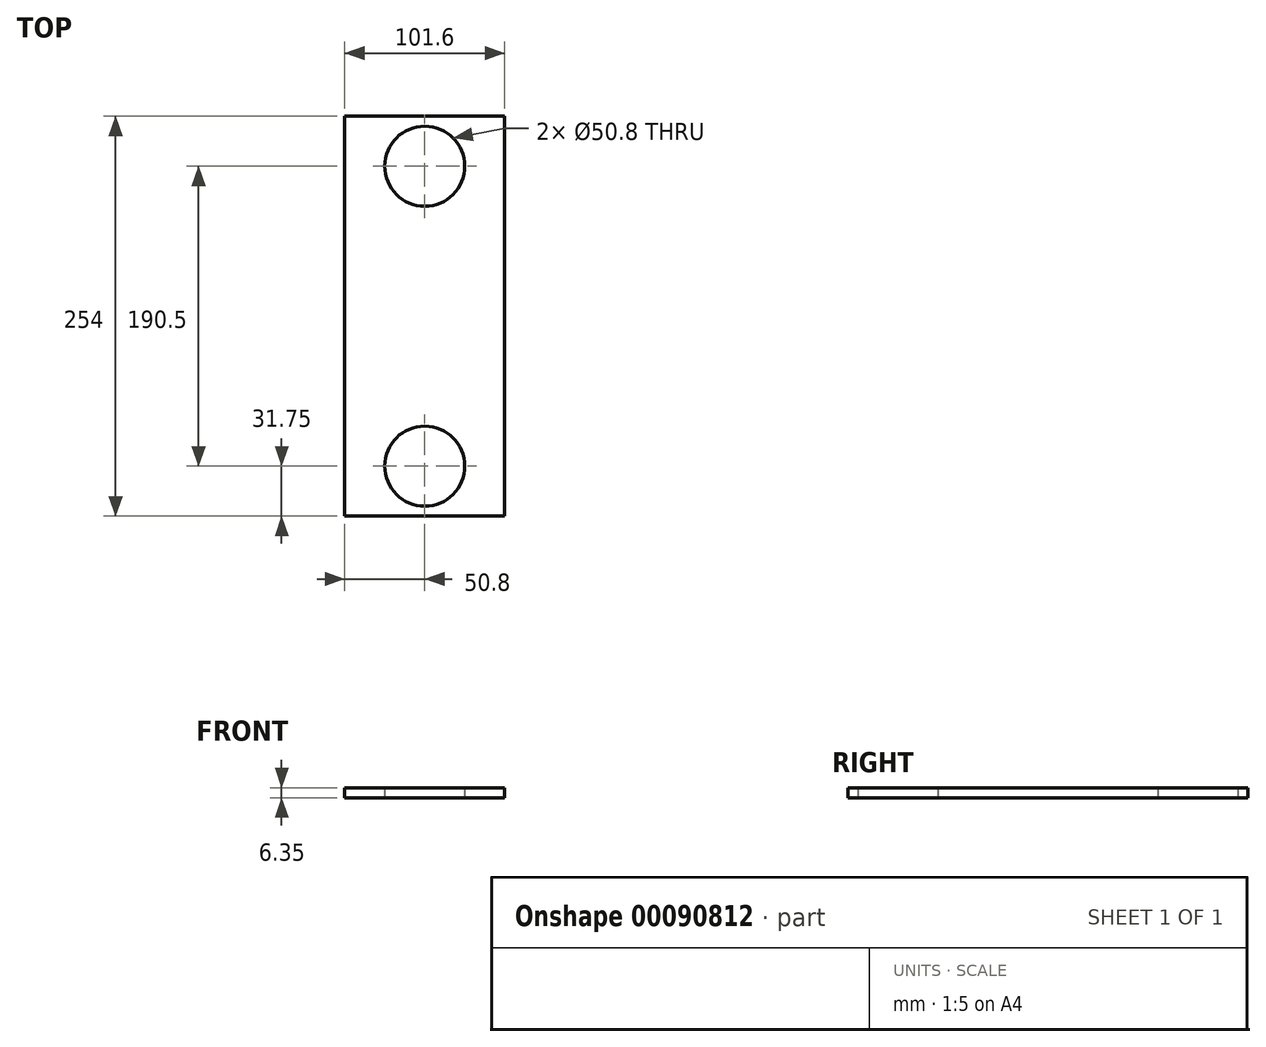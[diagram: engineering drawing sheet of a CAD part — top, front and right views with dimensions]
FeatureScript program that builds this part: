
annotation { "Feature Type Name" : "Feature", "Feature Type Description" : "" }
export const myFeature = defineFeature(function(context is Context, id is Id, definition is map)
    precondition{}
    {
        {
            var Q0;
            Q0=qCreatedBy(makeId("Top.planeOp"),FACE);
            var sketch = newSketch(context, id + "F0", { "sketchPlane" : qUnion([Q0])});
            skLineSegment(sketch, "E0.bottom", {"start": v(-37.93, 151.23) * mm, "end": v(63.67, 151.23) * mm});
            skLineSegment(sketch, "E0.top", {"start": v(-37.93, -102.77) * mm, "end": v(63.67, -102.77) * mm});
            skLineSegment(sketch, "E0.left", {"start": v(-37.93, 151.23) * mm, "end": v(-37.93, -102.77) * mm});
            skLineSegment(sketch, "E0.right", {"start": v(63.67, 151.23) * mm, "end": v(63.67, -102.77) * mm});
            skPoint(sketch, "E1", {"position": v(12.87, 151.23) * mm});
            skCircle(sketch, "E2", {"center": v(12.87, 119.48) * mm, "radius": 25.4 * mm});
            skCircle(sketch, "E3", {"center": v(12.87, -71.02) * mm, "radius": 25.4 * mm});
            skSolve(sketch);
        }
        {
            var Q0;
            Q0 = qSketchRegion(id + "F0", true);
            extrude(context, id + "F1", {"entities" : qUnion([Q0]), "depth" : 6.35 * mm});
        }
    });
